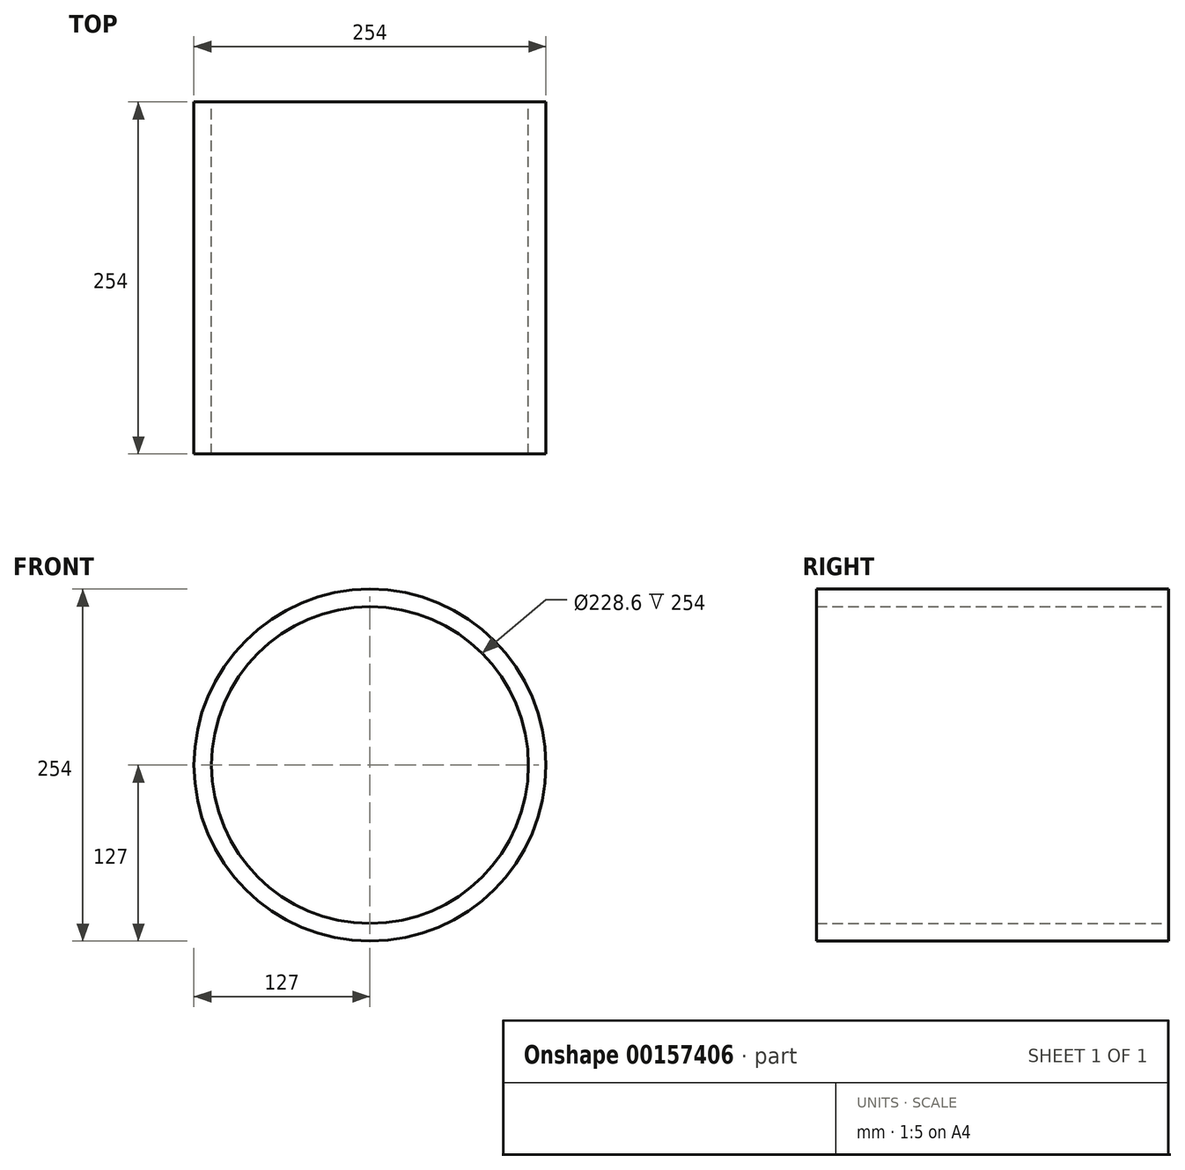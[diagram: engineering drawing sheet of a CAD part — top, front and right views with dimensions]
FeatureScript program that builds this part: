
annotation { "Feature Type Name" : "Feature", "Feature Type Description" : "" }
export const myFeature = defineFeature(function(context is Context, id is Id, definition is map)
    precondition{}
    {
        {
            var Q0;
            Q0=qCreatedBy(makeId("Front.planeOp"),FACE);
            var sketch = newSketch(context, id + "F0", { "sketchPlane" : qUnion([Q0])});
            skCircle(sketch, "E0", {"center": v(0, 0) * mm, "radius": 127 * mm});
            skCircle(sketch, "E1", {"center": v(0, 0) * mm, "radius": 114.3 * mm});
            skSolve(sketch);
        }
        {
            var Q0;
            Q0 = qSketchRegion(id + "F0", true);
            extrude(context, id + "F1", {"entities" : qUnion([Q0]), "depth" : 254 * mm});
        }
    });
